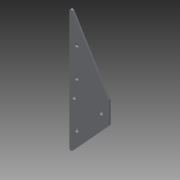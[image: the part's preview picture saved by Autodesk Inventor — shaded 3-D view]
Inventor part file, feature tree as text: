
AUTODESK INVENTOR PART (.ipt)
format: ipt  version: 2013 (Build 170138000, 138)  size: 122,880 bytes
history: native  units: in
note: dims shown in document units (in); Inventor stores cm internally (conversion verified against a paired STEP export)
features: extrude x5, sketch x5, fillet x3
ambient origin geometry x8: Origin, YZ Plane, XZ Plane, XY Plane, X Axis, Y Axis, Z Axis, Center Point
bodies: Solid1 (feature_tree)
feature tree (13):
  extrude  "Extrusion1"  Depth=6.0in
  extrude  "Extrusion2"  Depth=0.28in
  fillet  "Fillet1"  Radius=0.28in
  extrude  "Extrusion3"  Depth=0.5in
  fillet  "Fillet2"  Radius=0.56in
  fillet  "Fillet3"  Radius=0.31in
  extrude  "Extrusion4"  Depth=0.125in
  extrude  "Extrusion5"  Depth=0.266in
  sketch  "Sketch1"  dims[d1=1.5in d2=6.0in]
  sketch  "Sketch2"  dims[d3=0.125in d4=0.0in d5=0.28in d6=0.28in]
  sketch  "Sketch3"  dims[d7=0.5in d8=0.5in d9=0.56in d11=0.31in]
  sketch  "Sketch4"  dims[d12=1.0in d13=0.0in d14=0.125in]
  sketch  "Sketch5"  dims[d15=0.266in d16=0.266in d17=0.5in d18=0.5in d19=1.737in d20=2.0in d21=1.0in d22=0.0in d23=0.125in d24=3.0in d25=2.75in d26=2.75in d27=0.125in d28=0.266in d29=3.125in d30=0.5in d31=1.0in d32=0.0in d33=1.0in d34=0.0in]
